# Revit family: NaughtOne_SymbolSingleSeatWork
name_source: partatom
category: Furniture
units: mm (PartAtom-declared; Revit-internal decimal feet)

## family parameters
Always vertical = Yes
Cut with Voids When Loaded = No
Enable Cutting in Views = No
OmniClass Number = 23.40.20.00
OmniClass Title = General Furniture and Specialties
Render Appearance Source = Family Geometry
Room Calculation Point = No
Shared = Yes
Work Plane-Based = No

## types (7) — shared parameters
Assembly Code = E2020200
Manufacturer = Herman Miller, Inc.
Package Qty = 1
URL = http://www.hermanmiller.com
zero-valued in all types: Default Elevation

## per-type parameters (varying)
| type | Description | Foot aux 1 | Foot aux 2 | Model | Seat Bench Single Fabric | Seat No Arms Single and Multiple Fabric | Seat One Arm CornerSingle and Multiple Fabric | Seat Two Arms Single and Multiple Fabric | Seat aux 1 | Seat aux 2 | Type |
| Seat Bench Single Fabric Work Ht | Symbol Single Seat Bench Work height 18 inch seat height Single Fabric | 9.634 " | 9.634 " | NOSYN110W1 | Yes | No | No | No | 15 " | 15 " | 1 |
| Seat No Arms Single Fabric Work Ht | Symbol Single Seat No Arms Work height 18 inch seat height Single Fabric | 9.7 " | 13.4 " | NOSYN120W1 | No | Yes | No | No | 18.7 " | 15.1 " | 2 |
| Seat No Arms Multiple Fabric Work Ht | Symbol Single Seat No Arms Work height 18 inch seat height Multiple Fabric | 9.7 " | 13.4 " | NOSYN120W2 | No | Yes | No | No | 18.7 " | 15.1 " | 3 |
| Seat One Arm Corner Single Fabric Work Ht | Symbol Single Seat One Arm Work height 18 inch seat height Corner Single Fabric | 13.2 " | 13.2 " | NOSYN130W1 | No | No | Yes | No | 18.5 " | 11.5 " | 4 |
| Seat One Arm Corner Multiple Fabric Work Ht | Symbol Single Seat One Arm Work height 18 inch seat height Corner Multiple Fabric | 13.2 " | 13.2 " | NOSYN130W2 | No | No | Yes | No | 18.5 " | 11.5 " | 5 |
| Seat Two Arms Single Fabric Work Ht | Symbol Single Seat Two Arms Work height 18 inch seat height Single Fabric | 16.7 " | 13.2 " | NOSYN140W1 | No | No | No | Yes | 18.6 " | 15 " | 6 |
| Seat Two Arms Multiple Fabric Work Ht | Symbol Single Seat Two Arms Work height 18 inch seat height Multiple Fabric | 16.7 " | 13.2 " | NOSYN140W2 | No | No | No | Yes | 18.6 " | 15 " | 7 |

## geometry (parser evidence)
native form markers: Sweep x9
no freeform markers — native parametric forms only
